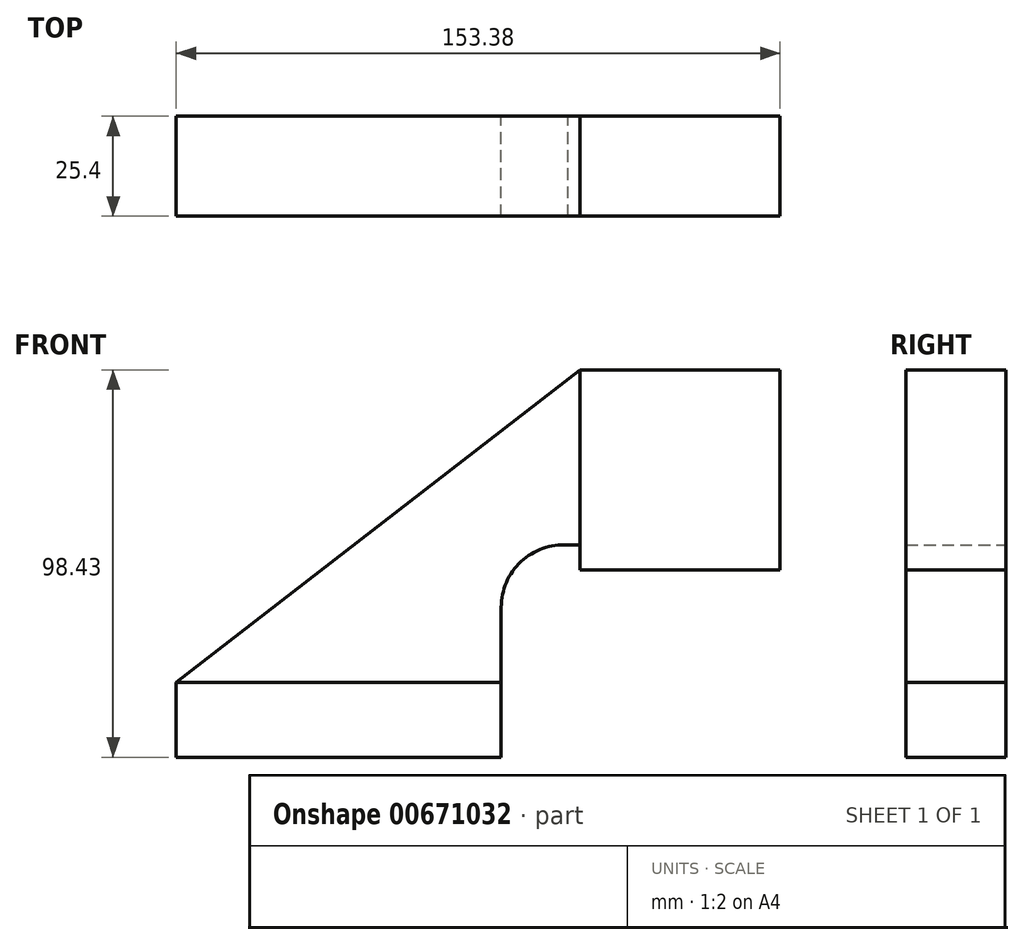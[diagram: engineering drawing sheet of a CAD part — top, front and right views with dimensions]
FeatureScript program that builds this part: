
annotation { "Feature Type Name" : "Feature", "Feature Type Description" : "" }
export const myFeature = defineFeature(function(context is Context, id is Id, definition is map)
    precondition{}
    {
        {
            var Q0;
            Q0=qCreatedBy(makeId("Front.planeOp"),FACE);
            var sketch = newSketch(context, id + "F0", { "sketchPlane" : qUnion([Q0])});
            skLineSegment(sketch, "E0.bottom", {"start": v(-41.28, 9.52) * mm, "end": v(41.27, 9.53) * mm});
            skLineSegment(sketch, "E0.top", {"start": v(-41.27, -9.53) * mm, "end": v(41.28, -9.53) * mm});
            skLineSegment(sketch, "E0.left", {"start": v(-41.28, 9.52) * mm, "end": v(-41.27, -9.53) * mm});
            skLineSegment(sketch, "E0.right", {"start": v(41.28, 9.53) * mm, "end": v(41.28, -9.52) * mm});
            skPoint(sketch, "E0.middle", {"position": v(0, 0) * mm});
            skLineSegment(sketch, "E1.bottom", {"start": v(61.3, 88.9) * mm, "end": v(112.1, 88.9) * mm});
            skLineSegment(sketch, "E1.top", {"start": v(61.3, 38.1) * mm, "end": v(112.1, 38.1) * mm});
            skLineSegment(sketch, "E1.left", {"start": v(61.3, 88.9) * mm, "end": v(61.3, 38.1) * mm});
            skLineSegment(sketch, "E1.right", {"start": v(112.1, 88.9) * mm, "end": v(112.1, 38.1) * mm});
            skPoint(sketch, "E1.middle", {"position": v(86.7, 63.5) * mm});
            skLineSegment(sketch, "E2", {"start": v(41.27, 9.53) * mm, "end": v(41.27, 28.58) * mm});
            skLineSegment(sketch, "E3", {"start": v(41.28, 28.57) * mm, "end": v(41.28, 28.57) * mm});
            skArc(sketch, "E4", {"start": v(41.28, 28.57) * mm, "mid": v(46.3, 40.17) * mm, "end": v(58.21, 44.41) * mm});
            skLineSegment(sketch, "E5", {"start": v(58.21, 44.41) * mm, "end": v(102.66, 44.41) * mm});
            skLineSegment(sketch, "E6", {"start": v(-41.28, 9.52) * mm, "end": v(61.3, 88.9) * mm});
            skSolve(sketch);
        }
        {
            var Q0;
            Q0=makeQuery(id+"F0.imprint","IMPRINT",FACE,{"disambiguationData":[TD([[makeQuery(id+"F0.imprint","IMPRINT",EDGE,{"derivedFrom":sQuery(id+"F0.wireOp",EDGE,"E0.bottom")}),-1.0]])]});
            var Q1;
            {var subQ0=sQuery(id+"F0.wireOp",EDGE,"E1.bottom");Q1=makeQuery(id+"F0.imprint","IMPRINT",FACE,{"disambiguationData":[TD([[makeQuery(id+"F0.imprint","IMPRINT",EDGE,{"derivedFrom":subQ0}),-1.0]])]});}
            extrude(context, id + "F1", {"entities" : qUnion([Q0, Q1]), "depth" : 25.4 * mm, "offsetDistance" : 25.4 * mm});
        }
        {
            var Q0;
            Q0 = qSketchRegion(id + "F0", true);
            extrude(context, id + "F2", {"entities" : qUnion([Q0]), "depth" : 25.4 * mm, "offsetDistance" : 25.4 * mm});
        }
    });
